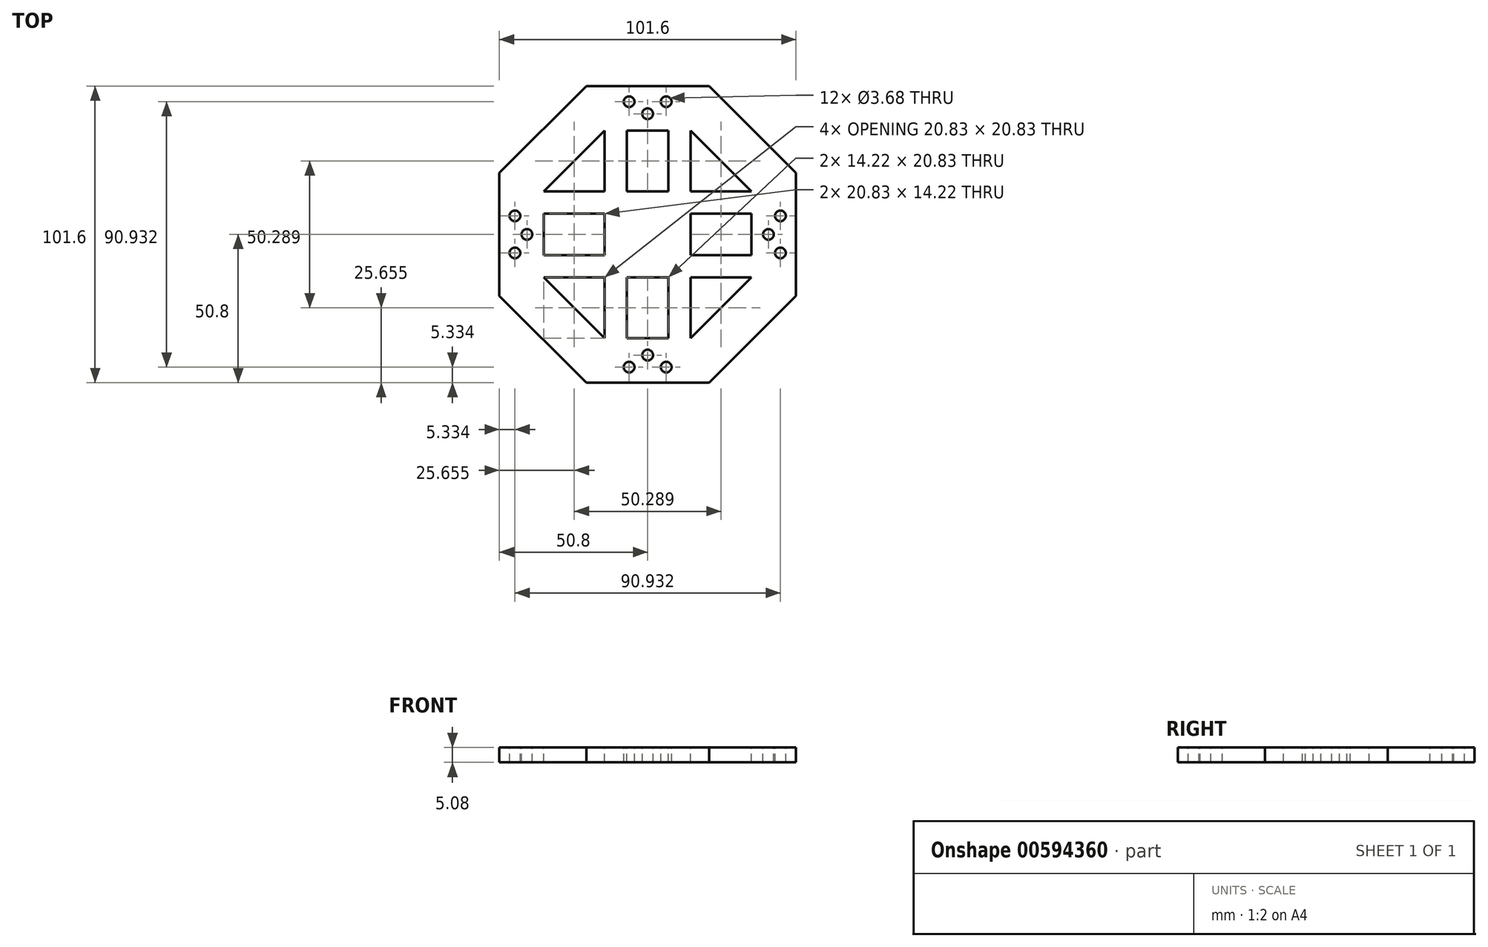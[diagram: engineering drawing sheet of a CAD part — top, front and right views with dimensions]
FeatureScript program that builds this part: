
annotation { "Feature Type Name" : "Feature", "Feature Type Description" : "" }
export const myFeature = defineFeature(function(context is Context, id is Id, definition is map)
    precondition{}
    {
        {
            var Q0;
            Q0=qCreatedBy(makeId("Top.planeOp"),FACE);
            var sketch = newSketch(context, id + "F0", { "sketchPlane" : qUnion([Q0])});
            skCircle(sketch, "E0.cCircle", {"center": v(0, 0) * mm, "radius": 50.8 * mm, "construction": true});
            skLineSegment(sketch, "E0.0", {"start": v(-21.04, 50.8) * mm, "end": v(21.04, 50.8) * mm});
            skLineSegment(sketch, "E0.1", {"start": v(21.04, 50.8) * mm, "end": v(50.8, 21.04) * mm});
            skLineSegment(sketch, "E0.2", {"start": v(50.8, 21.04) * mm, "end": v(50.8, -21.04) * mm});
            skLineSegment(sketch, "E0.3", {"start": v(50.8, -21.04) * mm, "end": v(21.04, -50.8) * mm});
            skLineSegment(sketch, "E0.4", {"start": v(21.04, -50.8) * mm, "end": v(-21.04, -50.8) * mm});
            skLineSegment(sketch, "E0.5", {"start": v(-21.04, -50.8) * mm, "end": v(-50.8, -21.04) * mm});
            skLineSegment(sketch, "E0.6", {"start": v(-50.8, -21.04) * mm, "end": v(-50.8, 21.04) * mm});
            skLineSegment(sketch, "E0.7", {"start": v(-50.8, 21.04) * mm, "end": v(-21.04, 50.8) * mm});
            skPoint(sketch, "E0.0.midPoint", {"position": v(0, 50.8) * mm});
            skSolve(sketch);
        }
        {
            var Q0;
            Q0 = qSketchRegion(id + "F0", true);
            extrude(context, id + "F1", {"entities" : qUnion([Q0]), "depth" : 5.08 * mm, "offsetDistance" : 25.4 * mm});
        }
        {
            var Q0;
            Q0=makeQuery(id+"F1.opExtrude","CAP_FACE",FACE,{"disambiguationData":[OSD([sQuery(id+"F0.wireOp",EDGE,"E0.0"),sQuery(id+"F0.wireOp",EDGE,"E0.1"),sQuery(id+"F0.wireOp",EDGE,"E0.2"),sQuery(id+"F0.wireOp",EDGE,"E0.3"),sQuery(id+"F0.wireOp",EDGE,"E0.4"),sQuery(id+"F0.wireOp",EDGE,"E0.5"),sQuery(id+"F0.wireOp",EDGE,"E0.6"),sQuery(id+"F0.wireOp",EDGE,"E0.7")])],"isStart":false});
            var sketch = newSketch(context, id + "F2", { "sketchPlane" : qUnion([Q0])});
            skCircle(sketch, "E1.cCircle", {"center": v(0, 0) * mm, "radius": 35.56 * mm, "construction": true});
            skLineSegment(sketch, "E1.0", {"start": v(-14.73, 35.56) * mm, "end": v(14.73, 35.56) * mm});
            skLineSegment(sketch, "E1.1", {"start": v(14.73, 35.56) * mm, "end": v(35.56, 14.73) * mm});
            skLineSegment(sketch, "E1.2", {"start": v(35.56, 14.73) * mm, "end": v(35.56, -14.73) * mm});
            skLineSegment(sketch, "E1.3", {"start": v(35.56, -14.73) * mm, "end": v(14.73, -35.56) * mm});
            skLineSegment(sketch, "E1.4", {"start": v(14.73, -35.56) * mm, "end": v(-14.73, -35.56) * mm});
            skLineSegment(sketch, "E1.5", {"start": v(-14.73, -35.56) * mm, "end": v(-35.56, -14.73) * mm});
            skLineSegment(sketch, "E1.6", {"start": v(-35.56, -14.73) * mm, "end": v(-35.56, 14.73) * mm});
            skLineSegment(sketch, "E1.7", {"start": v(-35.56, 14.73) * mm, "end": v(-14.73, 35.56) * mm});
            skPoint(sketch, "E1.0.midPoint", {"position": v(0, 35.56) * mm});
            skSolve(sketch);
        }
        {
            var Q0;
            Q0 = qSketchRegion(id + "F2", true);
            extrude(context, id + "F3", {"entities" : qUnion([Q0]), "operationType" : NewBodyOperationType.REMOVE, "endBound" : BoundingType.THROUGH_ALL, "oppositeDirection" : true, "depth" : 25.4 * mm, "offsetDistance" : 25.4 * mm});
        }
        {
            var Q0;
            Q0=makeQuery(id+"F1.opExtrude","CAP_FACE",FACE,{"disambiguationData":[OSD([sQuery(id+"F0.wireOp",EDGE,"E0.0"),sQuery(id+"F0.wireOp",EDGE,"E0.1"),sQuery(id+"F0.wireOp",EDGE,"E0.2"),sQuery(id+"F0.wireOp",EDGE,"E0.3"),sQuery(id+"F0.wireOp",EDGE,"E0.4"),sQuery(id+"F0.wireOp",EDGE,"E0.5"),sQuery(id+"F0.wireOp",EDGE,"E0.6"),sQuery(id+"F0.wireOp",EDGE,"E0.7")])],"isStart":false});
            var sketch = newSketch(context, id + "F4", { "sketchPlane" : qUnion([Q0])});
            skLineSegment(sketch, "E2.bottom", {"start": v(-14.73, 35.56) * mm, "end": v(-7.1, 35.56) * mm});
            skLineSegment(sketch, "E2.top", {"start": v(-14.73, -35.56) * mm, "end": v(-7.1, -35.56) * mm});
            skLineSegment(sketch, "E2.left", {"start": v(-14.73, 35.56) * mm, "end": v(-14.73, -35.56) * mm});
            skLineSegment(sketch, "E2.right", {"start": v(-7.1, 35.56) * mm, "end": v(-7.1, -35.56) * mm});
            skLineSegment(sketch, "E3.bottom", {"start": v(14.73, 35.56) * mm, "end": v(7.1, 35.56) * mm});
            skLineSegment(sketch, "E3.top", {"start": v(14.73, -35.56) * mm, "end": v(7.1, -35.56) * mm});
            skLineSegment(sketch, "E3.left", {"start": v(14.73, 35.56) * mm, "end": v(14.73, -35.56) * mm});
            skLineSegment(sketch, "E3.right", {"start": v(7.1, 35.56) * mm, "end": v(7.1, -35.56) * mm});
            skLineSegment(sketch, "E4.bottom", {"start": v(-35.56, 14.73) * mm, "end": v(35.56, 14.73) * mm});
            skLineSegment(sketch, "E4.top", {"start": v(-35.56, 7.1) * mm, "end": v(35.56, 7.1) * mm});
            skLineSegment(sketch, "E4.left", {"start": v(-35.56, 14.73) * mm, "end": v(-35.56, 7.1) * mm});
            skLineSegment(sketch, "E4.right", {"start": v(35.56, 14.73) * mm, "end": v(35.56, 7.1) * mm});
            skLineSegment(sketch, "E5.bottom", {"start": v(-35.56, -14.73) * mm, "end": v(35.56, -14.73) * mm});
            skLineSegment(sketch, "E5.top", {"start": v(-35.56, -7.1) * mm, "end": v(35.56, -7.1) * mm});
            skLineSegment(sketch, "E5.left", {"start": v(-35.56, -14.73) * mm, "end": v(-35.56, -7.1) * mm});
            skLineSegment(sketch, "E5.right", {"start": v(35.56, -14.73) * mm, "end": v(35.56, -7.1) * mm});
            skSolve(sketch);
        }
        {
            var Q0;
            Q0 = qSketchRegion(id + "F4", true);
            extrude(context, id + "F5", {"entities" : qUnion([Q0]), "operationType" : NewBodyOperationType.ADD, "depth" : -5.08 * mm, "offsetDistance" : 25.4 * mm});
        }
        {
            var Q0;
            Q0=makeQuery(id+"F5.boolean.opBoolean","MERGE",FACE,{"derivedFrom":[makeQuery(id+"F1.opExtrude","CAP_FACE",FACE,{"disambiguationData":[OSD([sQuery(id+"F0.wireOp",EDGE,"E0.0"),sQuery(id+"F0.wireOp",EDGE,"E0.1"),sQuery(id+"F0.wireOp",EDGE,"E0.2"),sQuery(id+"F0.wireOp",EDGE,"E0.3"),sQuery(id+"F0.wireOp",EDGE,"E0.4"),sQuery(id+"F0.wireOp",EDGE,"E0.5"),sQuery(id+"F0.wireOp",EDGE,"E0.6"),sQuery(id+"F0.wireOp",EDGE,"E0.7")])],"isStart":false}),makeQuery(id+"F5.opExtrude","CAP_FACE",FACE,{"disambiguationData":[OSD([sQuery(id+"F4.wireOp",EDGE,"E2.bottom"),sQuery(id+"F4.wireOp",EDGE,"E2.top"),sQuery(id+"F4.wireOp",EDGE,"E2.left"),sQuery(id+"F4.wireOp",EDGE,"E2.right"),sQuery(id+"F4.wireOp",EDGE,"E3.bottom"),sQuery(id+"F4.wireOp",EDGE,"E3.top"),sQuery(id+"F4.wireOp",EDGE,"E3.left"),sQuery(id+"F4.wireOp",EDGE,"E3.right"),sQuery(id+"F4.wireOp",EDGE,"E4.bottom"),sQuery(id+"F4.wireOp",EDGE,"E4.top"),sQuery(id+"F4.wireOp",EDGE,"E4.left"),sQuery(id+"F4.wireOp",EDGE,"E4.right"),sQuery(id+"F4.wireOp",EDGE,"E5.bottom"),sQuery(id+"F4.wireOp",EDGE,"E5.top"),sQuery(id+"F4.wireOp",EDGE,"E5.left"),sQuery(id+"F4.wireOp",EDGE,"E5.right")])],"isStart":true})]});
            var sketch = newSketch(context, id + "F6", { "sketchPlane" : qUnion([Q0])});
            skCircle(sketch, "E6", {"center": v(45.47, 6.35) * mm, "radius": 1.84 * mm});
            skCircle(sketch, "E7", {"center": v(45.47, -6.35) * mm, "radius": 1.84 * mm});
            skCircle(sketch, "E8", {"center": v(41.35, 0) * mm, "radius": 1.84 * mm});
            skSolve(sketch);
        }
        {
            var Q0;
            Q0=makeQuery(id+"F5.boolean.opBoolean","MERGE",FACE,{"derivedFrom":[makeQuery(id+"F1.opExtrude","CAP_FACE",FACE,{"disambiguationData":[OSD([sQuery(id+"F0.wireOp",EDGE,"E0.0"),sQuery(id+"F0.wireOp",EDGE,"E0.1"),sQuery(id+"F0.wireOp",EDGE,"E0.2"),sQuery(id+"F0.wireOp",EDGE,"E0.3"),sQuery(id+"F0.wireOp",EDGE,"E0.4"),sQuery(id+"F0.wireOp",EDGE,"E0.5"),sQuery(id+"F0.wireOp",EDGE,"E0.6"),sQuery(id+"F0.wireOp",EDGE,"E0.7")])],"isStart":false}),makeQuery(id+"F5.opExtrude","CAP_FACE",FACE,{"disambiguationData":[OSD([sQuery(id+"F4.wireOp",EDGE,"E2.bottom"),sQuery(id+"F4.wireOp",EDGE,"E2.top"),sQuery(id+"F4.wireOp",EDGE,"E2.left"),sQuery(id+"F4.wireOp",EDGE,"E2.right"),sQuery(id+"F4.wireOp",EDGE,"E3.bottom"),sQuery(id+"F4.wireOp",EDGE,"E3.top"),sQuery(id+"F4.wireOp",EDGE,"E3.left"),sQuery(id+"F4.wireOp",EDGE,"E3.right"),sQuery(id+"F4.wireOp",EDGE,"E4.bottom"),sQuery(id+"F4.wireOp",EDGE,"E4.top"),sQuery(id+"F4.wireOp",EDGE,"E4.left"),sQuery(id+"F4.wireOp",EDGE,"E4.right"),sQuery(id+"F4.wireOp",EDGE,"E5.bottom"),sQuery(id+"F4.wireOp",EDGE,"E5.top"),sQuery(id+"F4.wireOp",EDGE,"E5.left"),sQuery(id+"F4.wireOp",EDGE,"E5.right")])],"isStart":true})]});
            var sketch = newSketch(context, id + "F7", { "sketchPlane" : qUnion([Q0])});
            skCircle(sketch, "E9", {"center": v(-6.36, 45.47) * mm, "radius": 1.84 * mm});
            skCircle(sketch, "E10", {"center": v(6.34, 45.47) * mm, "radius": 1.84 * mm});
            skCircle(sketch, "E11", {"center": v(0, 41.35) * mm, "radius": 1.84 * mm});
            skSolve(sketch);
        }
        {
            var Q0;
            Q0=makeQuery(id+"F5.boolean.opBoolean","MERGE",FACE,{"derivedFrom":[makeQuery(id+"F1.opExtrude","CAP_FACE",FACE,{"disambiguationData":[OSD([sQuery(id+"F0.wireOp",EDGE,"E0.0"),sQuery(id+"F0.wireOp",EDGE,"E0.1"),sQuery(id+"F0.wireOp",EDGE,"E0.2"),sQuery(id+"F0.wireOp",EDGE,"E0.3"),sQuery(id+"F0.wireOp",EDGE,"E0.4"),sQuery(id+"F0.wireOp",EDGE,"E0.5"),sQuery(id+"F0.wireOp",EDGE,"E0.6"),sQuery(id+"F0.wireOp",EDGE,"E0.7")])],"isStart":false}),makeQuery(id+"F5.opExtrude","CAP_FACE",FACE,{"disambiguationData":[OSD([sQuery(id+"F4.wireOp",EDGE,"E2.bottom"),sQuery(id+"F4.wireOp",EDGE,"E2.top"),sQuery(id+"F4.wireOp",EDGE,"E2.left"),sQuery(id+"F4.wireOp",EDGE,"E2.right"),sQuery(id+"F4.wireOp",EDGE,"E3.bottom"),sQuery(id+"F4.wireOp",EDGE,"E3.top"),sQuery(id+"F4.wireOp",EDGE,"E3.left"),sQuery(id+"F4.wireOp",EDGE,"E3.right"),sQuery(id+"F4.wireOp",EDGE,"E4.bottom"),sQuery(id+"F4.wireOp",EDGE,"E4.top"),sQuery(id+"F4.wireOp",EDGE,"E4.left"),sQuery(id+"F4.wireOp",EDGE,"E4.right"),sQuery(id+"F4.wireOp",EDGE,"E5.bottom"),sQuery(id+"F4.wireOp",EDGE,"E5.top"),sQuery(id+"F4.wireOp",EDGE,"E5.left"),sQuery(id+"F4.wireOp",EDGE,"E5.right")])],"isStart":true})]});
            var sketch = newSketch(context, id + "F8", { "sketchPlane" : qUnion([Q0])});
            skCircle(sketch, "E12", {"center": v(-45.47, -6.35) * mm, "radius": 1.84 * mm});
            skCircle(sketch, "E13", {"center": v(-45.47, 6.35) * mm, "radius": 1.84 * mm});
            skCircle(sketch, "E14", {"center": v(-41.35, 0) * mm, "radius": 1.84 * mm});
            skSolve(sketch);
        }
        {
            var Q0;
            Q0=makeQuery(id+"F5.boolean.opBoolean","MERGE",FACE,{"derivedFrom":[makeQuery(id+"F1.opExtrude","CAP_FACE",FACE,{"disambiguationData":[OSD([sQuery(id+"F0.wireOp",EDGE,"E0.0"),sQuery(id+"F0.wireOp",EDGE,"E0.1"),sQuery(id+"F0.wireOp",EDGE,"E0.2"),sQuery(id+"F0.wireOp",EDGE,"E0.3"),sQuery(id+"F0.wireOp",EDGE,"E0.4"),sQuery(id+"F0.wireOp",EDGE,"E0.5"),sQuery(id+"F0.wireOp",EDGE,"E0.6"),sQuery(id+"F0.wireOp",EDGE,"E0.7")])],"isStart":false}),makeQuery(id+"F5.opExtrude","CAP_FACE",FACE,{"disambiguationData":[OSD([sQuery(id+"F4.wireOp",EDGE,"E2.bottom"),sQuery(id+"F4.wireOp",EDGE,"E2.top"),sQuery(id+"F4.wireOp",EDGE,"E2.left"),sQuery(id+"F4.wireOp",EDGE,"E2.right"),sQuery(id+"F4.wireOp",EDGE,"E3.bottom"),sQuery(id+"F4.wireOp",EDGE,"E3.top"),sQuery(id+"F4.wireOp",EDGE,"E3.left"),sQuery(id+"F4.wireOp",EDGE,"E3.right"),sQuery(id+"F4.wireOp",EDGE,"E4.bottom"),sQuery(id+"F4.wireOp",EDGE,"E4.top"),sQuery(id+"F4.wireOp",EDGE,"E4.left"),sQuery(id+"F4.wireOp",EDGE,"E4.right"),sQuery(id+"F4.wireOp",EDGE,"E5.bottom"),sQuery(id+"F4.wireOp",EDGE,"E5.top"),sQuery(id+"F4.wireOp",EDGE,"E5.left"),sQuery(id+"F4.wireOp",EDGE,"E5.right")])],"isStart":true})]});
            var sketch = newSketch(context, id + "F9", { "sketchPlane" : qUnion([Q0])});
            skCircle(sketch, "E15", {"center": v(6.35, -45.47) * mm, "radius": 1.84 * mm});
            skCircle(sketch, "E16", {"center": v(-6.35, -45.47) * mm, "radius": 1.84 * mm});
            skCircle(sketch, "E17", {"center": v(0, -41.35) * mm, "radius": 1.84 * mm});
            skSolve(sketch);
        }
        {
            var Q0;
            Q0 = qSketchRegion(id + "F6", true);
            extrude(context, id + "F10", {"entities" : qUnion([Q0]), "operationType" : NewBodyOperationType.REMOVE, "endBound" : BoundingType.THROUGH_ALL, "oppositeDirection" : true, "depth" : 25.4 * mm, "offsetDistance" : 25.4 * mm});
        }
        {
            var Q0;
            Q0 = qSketchRegion(id + "F7", true);
            extrude(context, id + "F11", {"entities" : qUnion([Q0]), "operationType" : NewBodyOperationType.REMOVE, "endBound" : BoundingType.THROUGH_ALL, "oppositeDirection" : true, "depth" : 25.4 * mm, "offsetDistance" : 25.4 * mm});
        }
        {
            var Q0;
            Q0 = qSketchRegion(id + "F8", true);
            extrude(context, id + "F12", {"entities" : qUnion([Q0]), "operationType" : NewBodyOperationType.REMOVE, "endBound" : BoundingType.THROUGH_ALL, "oppositeDirection" : true, "depth" : 25.4 * mm, "offsetDistance" : 25.4 * mm});
        }
        {
            var Q0;
            Q0 = qSketchRegion(id + "F9", true);
            extrude(context, id + "F13", {"entities" : qUnion([Q0]), "operationType" : NewBodyOperationType.REMOVE, "endBound" : BoundingType.THROUGH_ALL, "oppositeDirection" : true, "depth" : 25.4 * mm, "offsetDistance" : 25.4 * mm});
        }
        {
            var Q0;
            Q0=makeQuery(id+"F5.boolean.opBoolean","MERGE",FACE,{"derivedFrom":[makeQuery(id+"F1.opExtrude","CAP_FACE",FACE,{"disambiguationData":[OSD([sQuery(id+"F0.wireOp",EDGE,"E0.0"),sQuery(id+"F0.wireOp",EDGE,"E0.1"),sQuery(id+"F0.wireOp",EDGE,"E0.2"),sQuery(id+"F0.wireOp",EDGE,"E0.3"),sQuery(id+"F0.wireOp",EDGE,"E0.4"),sQuery(id+"F0.wireOp",EDGE,"E0.5"),sQuery(id+"F0.wireOp",EDGE,"E0.6"),sQuery(id+"F0.wireOp",EDGE,"E0.7")])],"isStart":false}),makeQuery(id+"F5.opExtrude","CAP_FACE",FACE,{"disambiguationData":[OSD([sQuery(id+"F4.wireOp",EDGE,"E2.bottom"),sQuery(id+"F4.wireOp",EDGE,"E2.top"),sQuery(id+"F4.wireOp",EDGE,"E2.left"),sQuery(id+"F4.wireOp",EDGE,"E2.right"),sQuery(id+"F4.wireOp",EDGE,"E3.bottom"),sQuery(id+"F4.wireOp",EDGE,"E3.top"),sQuery(id+"F4.wireOp",EDGE,"E3.left"),sQuery(id+"F4.wireOp",EDGE,"E3.right"),sQuery(id+"F4.wireOp",EDGE,"E4.bottom"),sQuery(id+"F4.wireOp",EDGE,"E4.top"),sQuery(id+"F4.wireOp",EDGE,"E4.left"),sQuery(id+"F4.wireOp",EDGE,"E4.right"),sQuery(id+"F4.wireOp",EDGE,"E5.bottom"),sQuery(id+"F4.wireOp",EDGE,"E5.top"),sQuery(id+"F4.wireOp",EDGE,"E5.left"),sQuery(id+"F4.wireOp",EDGE,"E5.right")])],"isStart":true})]});
            var sketch = newSketch(context, id + "F14", { "sketchPlane" : qUnion([Q0])});
            skLineSegment(sketch, "E18.bottom", {"start": v(-7.1, -7.1) * mm, "end": v(7.1, -7.1) * mm});
            skLineSegment(sketch, "E18.top", {"start": v(-7.1, 7.1) * mm, "end": v(7.1, 7.1) * mm});
            skLineSegment(sketch, "E18.left", {"start": v(-7.1, -7.1) * mm, "end": v(-7.1, 7.1) * mm});
            skLineSegment(sketch, "E18.right", {"start": v(7.1, -7.1) * mm, "end": v(7.1, 7.1) * mm});
            skSolve(sketch);
        }
        {
            var Q0;
            Q0 = qSketchRegion(id + "F14", true);
            extrude(context, id + "F15", {"entities" : qUnion([Q0]), "operationType" : NewBodyOperationType.ADD, "depth" : -5.08 * mm, "offsetDistance" : 25.4 * mm});
        }
    });
